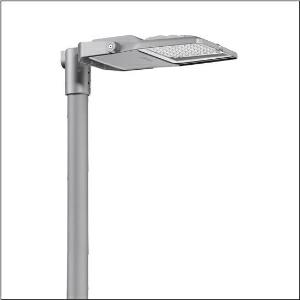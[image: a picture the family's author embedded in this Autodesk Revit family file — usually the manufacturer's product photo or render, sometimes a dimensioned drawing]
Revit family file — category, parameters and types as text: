
# Revit family: floodlight_fl_21_iq_mini___pl33t_5xa7772d2f3a_d038
name_source: partatom
category: Lighting Fixtures
units: mm (PartAtom-declared; Revit-internal decimal feet)

## family parameters
Cut with Voids When Loaded = No
Host = Face
Light Source = No
Part Type = Normal
Room Calculation Point = No
Round Connector Dimension = Use Diameter
Shared = No

## types (1)
- --- (1 x LED, 17620 lm, 143 W, 3000K)
    Apparent Load = 143 VA
    CIE Flux Codes = 26 75 99 100 100
    Color Rendering = 70
    Color Temperature = 3000K
    Default Elevation = 1800 mm
    Description = Floodlight FL 21 iQ mini, floodlight, primary light control with lens, of PMMA, primary optical cover: protective disc, of toughened safety glass, transparent, light distribution: PL33T, light emission: direct distribution, installation type: surface-mounted, LED, High Power LED, rated luminous flux: 17.620lm, luminous efficacy: 123lm/W, light colour: 730, colour temperature: 3000K, control: Auto-Match, Temp-Guard, Night-Set, Smart-Wire, Desk-Remote (wireless, voltage-free reading and setting of iQ features in the workshop via application-optimized NFC function/RFID function), optimised constant luminous flux control (CLO 2.0), Light-Fading, Lumen-Switch, with terminal, 6-pole, mains connection: 220..240V, AC, 50/60Hz, start of lifetime: 143W, end of service life: 152W, reduction: 61W, luminaire housing, of diecast aluminium, powder-coated, Siteco® metallic grey (DB 702S), corrosivity category C5 mid according to DIN EN ISO 12944, sealing non-destructively replaceable, please order mast flange separately, mast bracket, of steel, galvanised, powder-coated, protection rating (complete): IP66, insulation class (complete): insulation class II (safety insulation), certification: CE, ENEC, VDE, protection symbol: D, impact resistance: IK08, permissible operating ambient temperature: -40..+40°C, permissible operating ambient temperature for outdoor applications: -40..+50°C, standard: DIN EN 12944, LABS conformity tested according to VDMA 24364:2018-05, packaging unit: 1 piece

Light Distribution: PL33T
    Height = 70 mm
    Lamp = 1 x LED
    Lamp Light Flux = 17620 lm
    Lamp Power = 143 W
    Lamp count = 1
    Length = 485 mm
    Luminous efficacy = 123 lm/W
    Manufacturer = Siteco
    ModVariant = No
    Model = 5XA7772D2F3A
    Number of Poles = 1
    OnlyDefault = Yes
    Power Factor = 1
    Product Name = Floodlight FL 21 iQ mini | PL33T
    Product group = floodlight | pylon annexe
    ProductGroupID = 6200
    Protection Class = Protection class II
    Protection Degree = IP 66
    RLX_Detail_Level = 1
    RLX_Emergency_Light_Flux = 0 lm
    RLX_Emergency_Type = 0
    RLX_Emergency_Type_DB = No
    RlxData = <blob elided: 101441 chars, md5=db3036b9>
    Socket = socket
    Standby Power = 0 W
    System Light Flux = 17620 lm
    System Power = 143 W
    Type Comments = factory setting: luminous flux: 100 % | dim-lin: 254 | 730 mA
    Type Image = l_1007125.jpg
    URL = http://relux.com
    VarID = @adj_081415
    Voltage = 0 V
    Weight = 0.00 kg
    Width = 337 mm

## geometry (parser evidence)
native form markers: Blend x4, Sweep x13
no freeform markers — native parametric forms only
